# Revit family: PD3 FP types Sans hôte
name_source: partatom
category: Dispositifs d'éclairage
units: mm (PartAtom-declared; Revit-internal decimal feet)

## family parameters
Basée sur le plan de construction = Oui
Conserver l'orientation des annotations = Non
Cote de connecteur circulaire = Utiliser le diamètre
Couper avec des vides une fois chargée = Non
Partagée = Non
Point de calcul de pièce = Non
Toujours verticalement = Oui
Type d'élément = Normal

## types (6) — shared parameters
Alimentation = 110-240 V AC
Classe = II
Code d'assemblage = D5010200
Fabricant = B.E.G.
Hauteur de montage max = 300 cm
Image du type = 360°.jpg
Marque = LUXOMAT
Mode de pose = Faux Plafond
Température ambiante = -25°C at +50°C
URL = http://www.luxomat.com
zero-valued in all types: Elévation par défaut

## per-type parameters (varying)
| type | Charge Cos ɸ =0.5 | Charge Cos ɸ =1 | Charge LED | Commentaires du type | Consommation | IP | Modèle | Relais | Référence | Type de Sortie |
| 01- PD3 FP Générique |  |  |  | DET.MOUV.360°/Ø10M FAUX PLAFOND |  | 20 ou 23 | PD3 FP |  |  |  |
| 04- PD3N 1C MICRO FP réf 92184 | 1150 VA | 2300 W | 300 W | DET.MOUV.1 CONTACT + MICRO.360°/Ø10M FAUX PLAFOND | 0,25 W | 23 | PD3N 1C MICRO FP | 10 A | 92184 | TOR + Micro |
| 02- PD3N 1C FP réf 92196 | 1150 VA | 2300 W | 300 W | DET.MOUV.1 CONTACT.360°/Ø10M FAUX PLAFOND | 0,25 W | 23 | PD3N 1C FP | 10 A | 92196 | TOR |
| 06- PD3 1C FP réf 92197 | 1000 VA | 2000 W | 250 W | DET.MOUV.1 CONTACT.360°/Ø10M FAUX PLAFOND NON TELECOMMANDABLE | < 1W | 20 option capot IP 23 | PD3 1C FP | 8,7 A | 92197 | TOR |
| 03- PD3N 1C NO FP réf 92576 | 1150 VA | 2300 W | 300 W | DET.MOUV.1 CONTACT SEC NO.360°/Ø10M FAUX PLAFOND | 0,25 W | 23 | PD3N 1C NO FP | 10 A | 92576 | TOR |
| 05- PD3N 2C FP réf 92198 | 1150 VA | 2300 W | 300 W | DET.MOUV.2 CONTACTS.360°/Ø10M FAUX PLAFOND | 0,30 W | 23 | PD3N 2C FP | 10 A / 3 A | 92198 | TOR + CVC |
